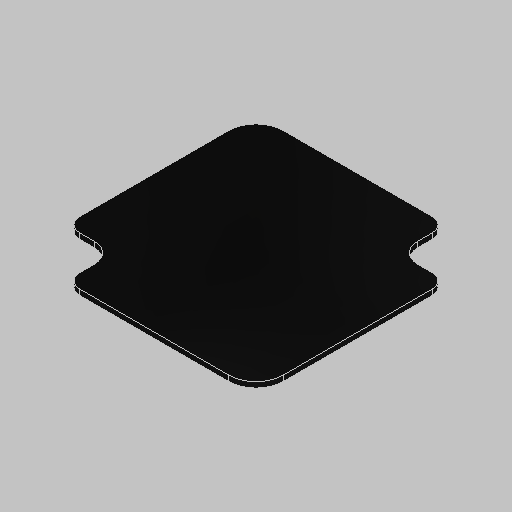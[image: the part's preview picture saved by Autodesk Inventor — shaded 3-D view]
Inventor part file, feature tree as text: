
AUTODESK INVENTOR PART (.ipt)
format: ipt  version: 2023.5 (Build 275446000, 446)  size: 70,144 bytes
history: native  units: mm (DEFAULTED — no unit token found)
features: fillet x1
ambient origin geometry x8: Origin, YZ Plane, XZ Plane, XY Plane, X Axis, Y Axis, Z Axis, Center Point
bodies: Solid1 (feature_tree)
feature tree (1):
  fillet  "Fillet3"  [1 undecoded]
note: 1 required parameter value undecoded (feature->parameter linkage not recoverable at this tier; creation-order binding heuristic only, values carry confidence <= 0.55)
